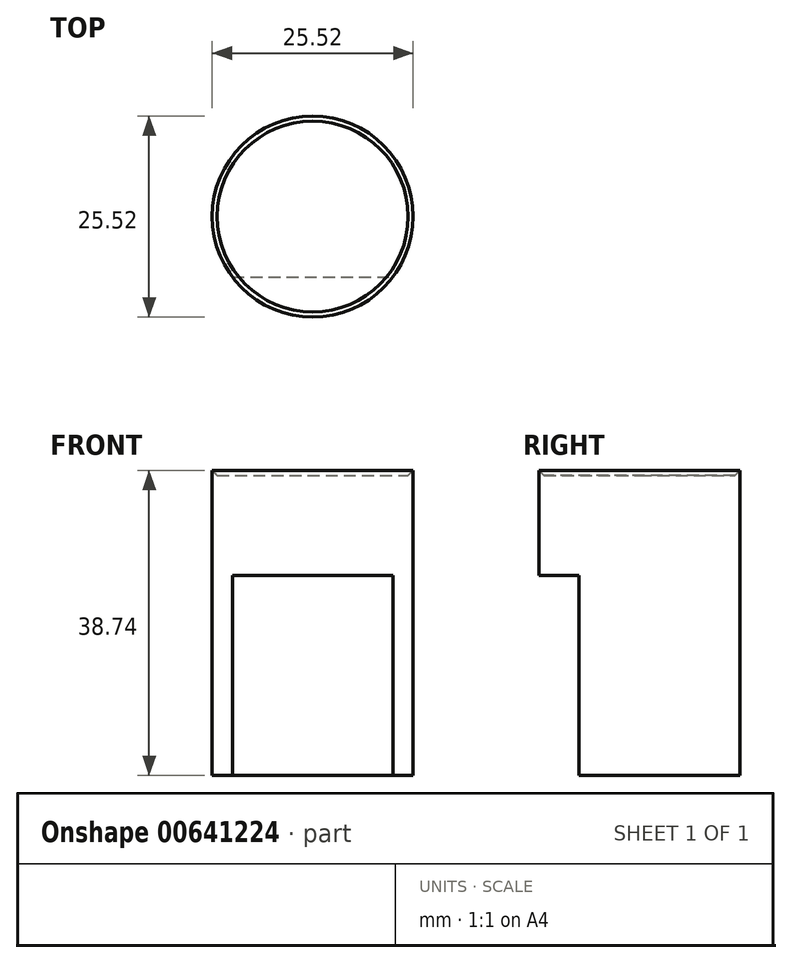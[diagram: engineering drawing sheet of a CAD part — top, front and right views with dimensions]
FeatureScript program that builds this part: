
annotation { "Feature Type Name" : "Feature", "Feature Type Description" : "" }
export const myFeature = defineFeature(function(context is Context, id is Id, definition is map)
    precondition{}
    {
        {
            var Q0;
            Q0=qCreatedBy(makeId("Front.planeOp"),FACE);
            var sketch = newSketch(context, id + "F0", { "sketchPlane" : qUnion([Q0])});
            skLineSegment(sketch, "E0", {"start": v(0, 0) * mm, "end": v(0, 12.7) * mm});
            skLineSegment(sketch, "E1", {"start": v(0, 12.7) * mm, "end": v(-12.76, 12.7) * mm});
            skLineSegment(sketch, "E2", {"start": v(-12.76, 12.7) * mm, "end": v(-12.76, 0) * mm});
            skLineSegment(sketch, "E3", {"start": v(-12.76, 0) * mm, "end": v(0, 0) * mm});
            skLineSegment(sketch, "E4", {"start": v(-12.76, 12.7) * mm, "end": v(-12.76, 13.33) * mm});
            skLineSegment(sketch, "E5", {"start": v(-12.76, 13.33) * mm, "end": v(-12.13, 12.7) * mm});
            skSolve(sketch);
        }
        {
            var Q0;
            Q0 = qSketchRegion(id + "F0", true);
            var Q1;
            Q1=sQuery(id+"F0.wireOp",EDGE,"E0");
            revolve(context, id + "F1", {"entities" : qUnion([Q0]), "axis" : qUnion([Q1]), "revolveType" : RevolveType.FULL});
        }
        {
            var Q0;
            Q0=makeQuery(id+"F1.opRevolve","SWEPT_FACE",FACE,{"disambiguationData":[OSD([sQuery(id+"F0.wireOp",EDGE,"E3")])]});
            var sketch = newSketch(context, id + "F2", { "sketchPlane" : qUnion([Q0])});
            skArc(sketch, "E6", {"start": v(-10.2, 7.68) * mm, "mid": v(0, -12.76) * mm, "end": v(10.2, 7.68) * mm});
            skLineSegment(sketch, "E7", {"start": v(-10.2, 7.68) * mm, "end": v(10.2, 7.68) * mm});
            skSolve(sketch);
        }
        {
            var Q0;
            Q0 = qSketchRegion(id + "F2", true);
            extrude(context, id + "F3", {"entities" : qUnion([Q0]), "operationType" : NewBodyOperationType.ADD, "depth" : 25.4 * mm, "offsetDistance" : 25.4 * mm});
        }
    });
